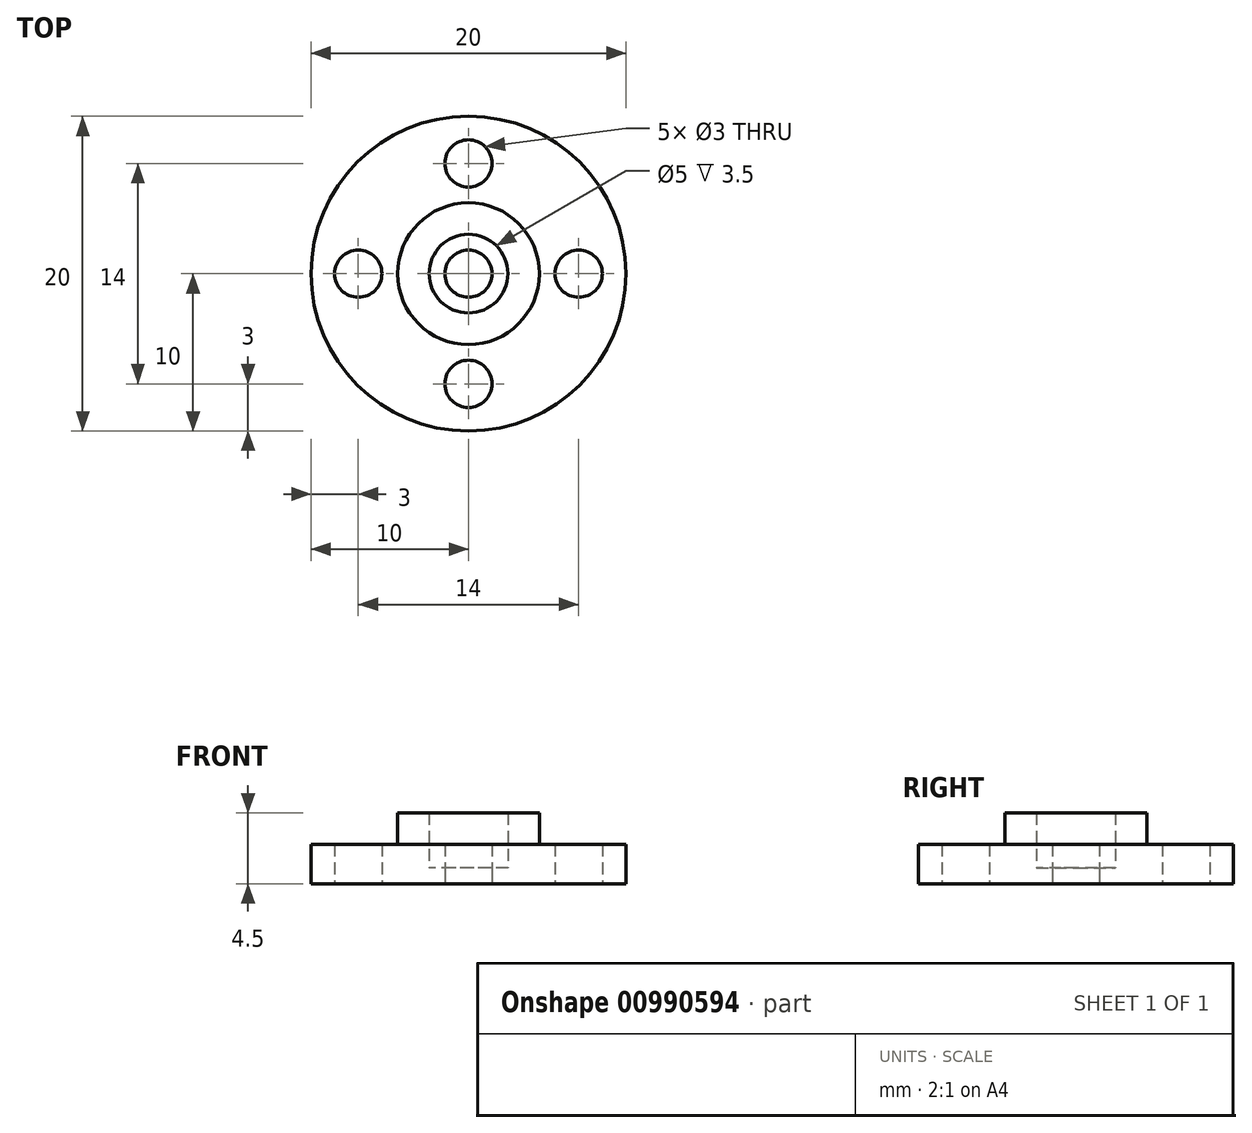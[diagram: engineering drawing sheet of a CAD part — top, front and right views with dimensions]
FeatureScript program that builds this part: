
annotation { "Feature Type Name" : "Feature", "Feature Type Description" : "" }
export const myFeature = defineFeature(function(context is Context, id is Id, definition is map)
    precondition{}
    {
        {
            var Q0;
            Q0=qCreatedBy(makeId("Top.planeOp"),FACE);
            var sketch = newSketch(context, id + "F0", { "sketchPlane" : qUnion([Q0])});
            skCircle(sketch, "E0", {"center": v(0, 0) * mm, "radius": 10 * mm});
            skSolve(sketch);
        }
        {
            var Q0;
            Q0=qSketchRegion(id+"F0",true);
            extrude(context, id + "F1", {"entities" : qUnion([Q0]), "depth" : 2.5 * mm, "offsetDistance" : 25 * mm});
        }
        {
            var Q0;
            Q0=makeQuery(id+"F1.opExtrude","CAP_FACE",FACE,{"disambiguationData":[OSD([sQuery(id+"F0.wireOp",EDGE,"E0")])],"isStart":false});
            var sketch = newSketch(context, id + "F2", { "sketchPlane" : qUnion([Q0])});
            skCircle(sketch, "E1", {"center": v(0, 0) * mm, "radius": 4.5 * mm});
            skCircle(sketch, "E2.0", {"center": v(0, 0) * mm, "radius": 2.5 * mm});
            skSolve(sketch);
        }
        {
            var Q0;
            Q0=qSketchRegion(id+"F2",true);
            extrude(context, id + "F3", {"entities" : qUnion([Q0]), "operationType" : NewBodyOperationType.ADD, "depth" : 2 * mm, "offsetDistance" : 25 * mm});
        }
        {
            var Q0;
            Q0=makeQuery(id+"F3.boolean.opBoolean","SPLIT",FACE,{"disambiguationData":[TD([makeQuery(id+"F3.opExtrude","SWEPT_FACE",FACE,{"disambiguationData":[OSD([sQuery(id+"F2.wireOp",EDGE,"E2.0")])]})])],"derivedFrom":makeQuery(id+"F1.opExtrude","CAP_FACE",FACE,{"disambiguationData":[OSD([sQuery(id+"F0.wireOp",EDGE,"E0")])],"isStart":false})});
            extrude(context, id + "F4", {"entities" : qUnion([Q0]), "operationType" : NewBodyOperationType.REMOVE, "oppositeDirection" : true, "depth" : 1.5 * mm, "offsetDistance" : 25 * mm});
        }
        {
            var Q0;
            Q0=makeQuery(id+"F1.opExtrude","CAP_FACE",FACE,{"disambiguationData":[OSD([sQuery(id+"F0.wireOp",EDGE,"E0")])],"isStart":true});
            var sketch = newSketch(context, id + "F5", { "sketchPlane" : qUnion([Q0])});
            skCircle(sketch, "E3", {"center": v(-7, 0) * mm, "radius": 1.5 * mm});
            skCircle(sketch, "E4.MirrorC", {"center": v(7, 0) * mm, "radius": 1.5 * mm});
            skCircle(sketch, "E5", {"center": v(0, -7) * mm, "radius": 1.5 * mm});
            skCircle(sketch, "E6.MirrorC", {"center": v(0, 7) * mm, "radius": 1.5 * mm});
            skCircle(sketch, "E7", {"center": v(0, 0) * mm, "radius": 1.5 * mm});
            skCircle(sketch, "E8", {"center": v(0, 0) * mm, "radius": 7 * mm, "construction": true});
            skSolve(sketch);
        }
        {
            var Q0;
            Q0=qSketchRegion(id+"F5",true);
            extrude(context, id + "F6", {"entities" : qUnion([Q0]), "operationType" : NewBodyOperationType.REMOVE, "oppositeDirection" : true, "depth" : 25 * mm, "offsetDistance" : 25 * mm});
        }
    });
